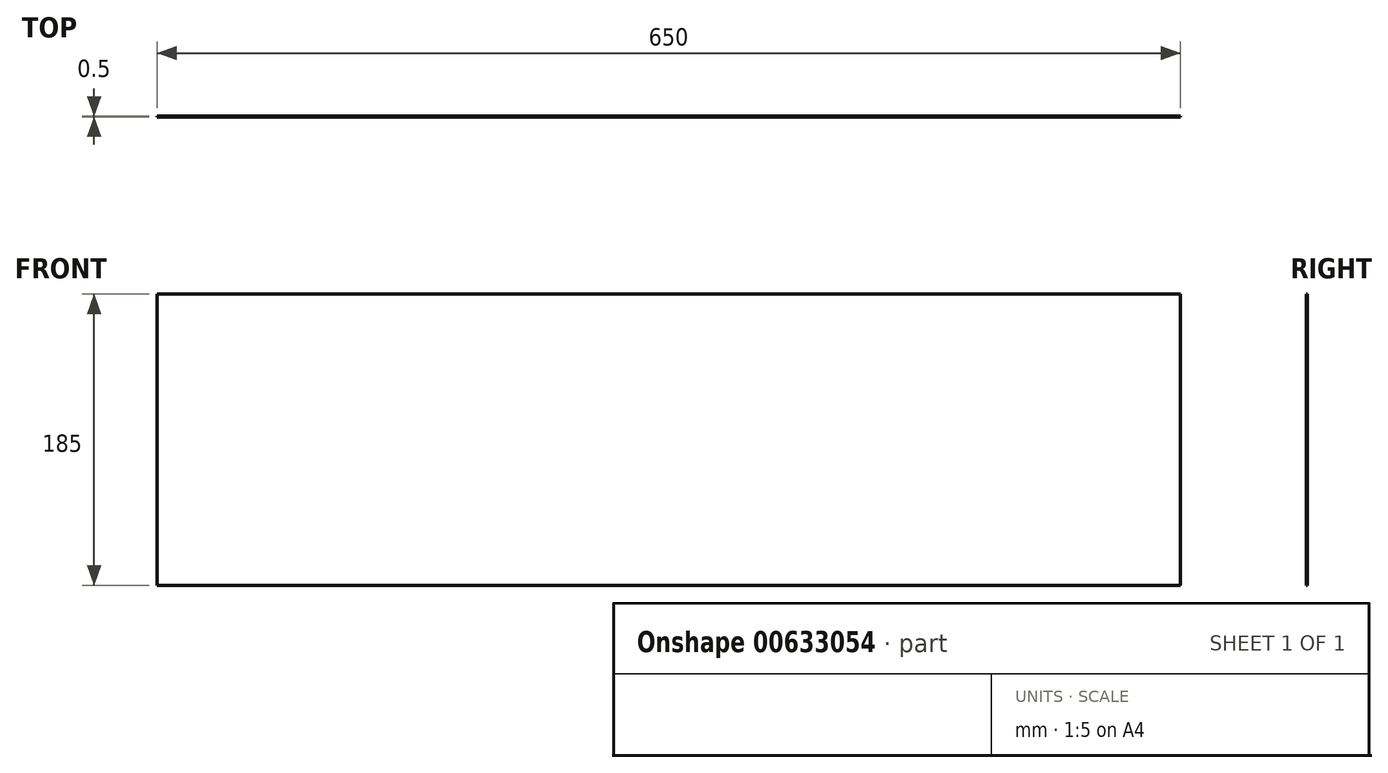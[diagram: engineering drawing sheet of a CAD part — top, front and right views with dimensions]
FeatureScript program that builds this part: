
annotation { "Feature Type Name" : "Feature", "Feature Type Description" : "" }
export const myFeature = defineFeature(function(context is Context, id is Id, definition is map)
    precondition{}
    {
        {
            var Q0;
            Q0=qCreatedBy(makeId("Front.planeOp"),FACE);
            var sketch = newSketch(context, id + "F0", { "sketchPlane" : qUnion([Q0])});
            skLineSegment(sketch, "E0.bottom", {"start": v(325, 92.5) * mm, "end": v(-325, 92.5) * mm});
            skLineSegment(sketch, "E0.top", {"start": v(325, -92.5) * mm, "end": v(-325, -92.5) * mm});
            skLineSegment(sketch, "E0.left", {"start": v(325, 92.5) * mm, "end": v(325, -92.5) * mm});
            skLineSegment(sketch, "E0.right", {"start": v(-325, 92.5) * mm, "end": v(-325, -92.5) * mm});
            skPoint(sketch, "E0.middle", {"position": v(0, 0) * mm});
            skSolve(sketch);
        }
        {
            var Q0;
            Q0=makeQuery(id+"F0.imprint","IMPRINT",FACE,{"disambiguationData":[TD([[makeQuery(id+"F0.imprint","IMPRINT",EDGE,{"derivedFrom":sQuery(id+"F0.wireOp",EDGE,"E0.bottom")}),1.0]])]});
            extrude(context, id + "F1", {"entities" : qUnion([Q0]), "depth" : 0.5 * mm, "offsetDistance" : 25 * mm});
        }
    });
